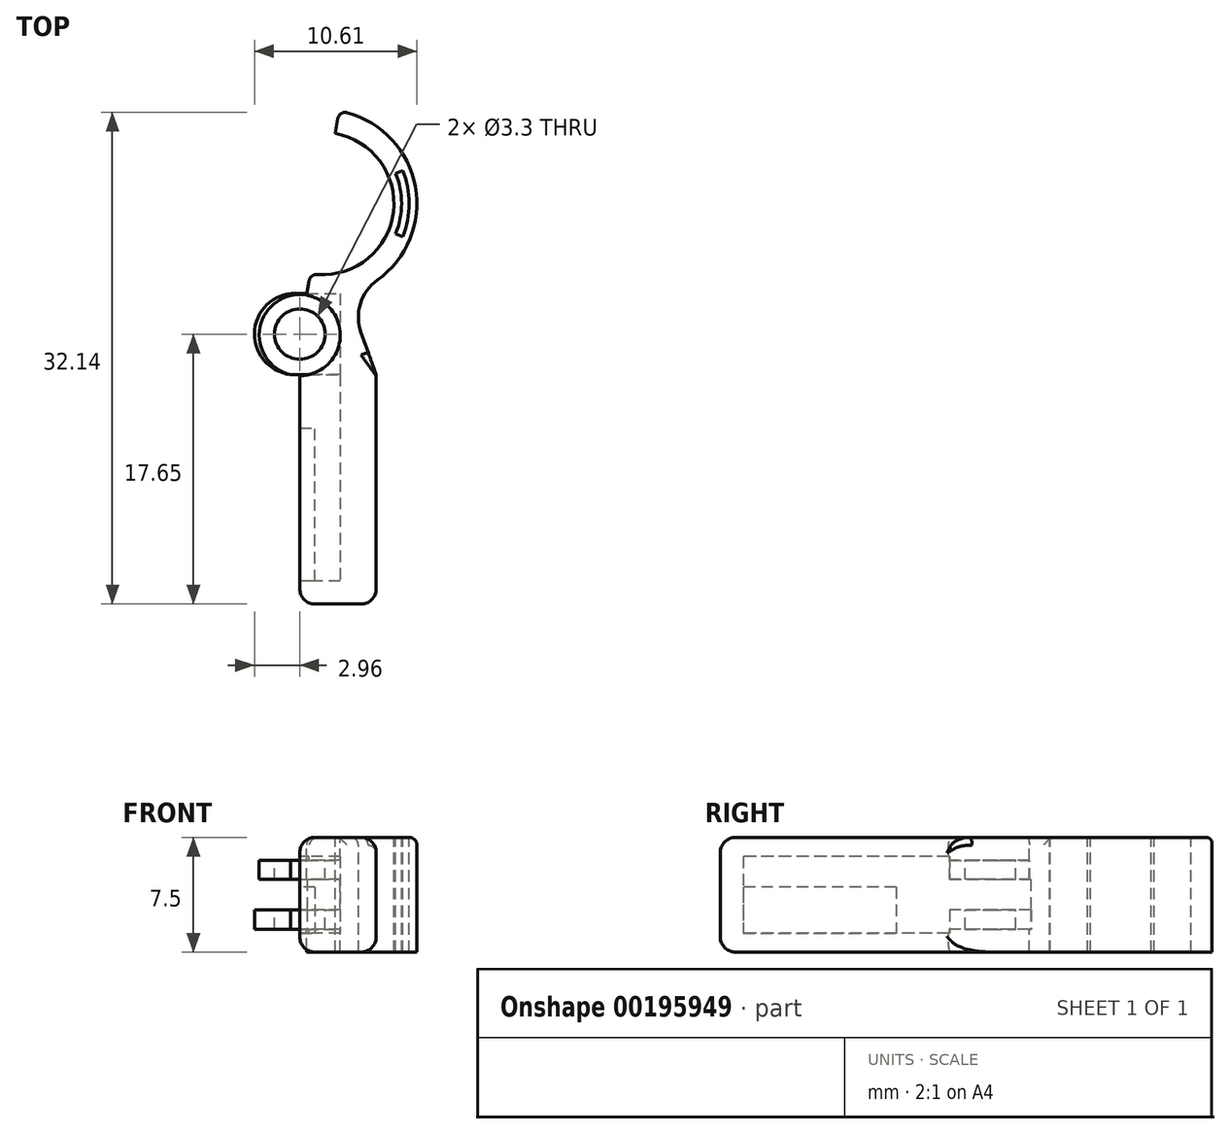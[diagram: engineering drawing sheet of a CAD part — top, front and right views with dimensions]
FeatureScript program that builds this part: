
annotation { "Feature Type Name" : "Feature", "Feature Type Description" : "" }
export const myFeature = defineFeature(function(context is Context, id is Id, definition is map)
    precondition{}
    {
        {
            var Q0;
            Q0=qCreatedBy(makeId("Front.planeOp"),FACE);
            var sketch = newSketch(context, id + "F0", { "sketchPlane" : qUnion([Q0])});
            skLineSegment(sketch, "E0.bottom", {"start": v(-2.5, 3.75) * mm, "end": v(2.5, 3.75) * mm});
            skLineSegment(sketch, "E0.top", {"start": v(-2.5, -3.75) * mm, "end": v(2.5, -3.75) * mm});
            skLineSegment(sketch, "E0.left", {"start": v(-2.5, 3.75) * mm, "end": v(-2.5, -3.75) * mm});
            skLineSegment(sketch, "E0.right", {"start": v(2.5, 3.75) * mm, "end": v(2.5, -3.75) * mm});
            skSolve(sketch);
        }
        {
            var Q0;
            Q0=makeQuery(id+"F0.imprint","IMPRINT",FACE,{"disambiguationData":[TD([[makeQuery(id+"F0.imprint","IMPRINT",EDGE,{"derivedFrom":sQuery(id+"F0.wireOp",EDGE,"E0.bottom")}),-1.0]])]});
            extrude(context, id + "F1", {"entities" : qUnion([Q0]), "oppositeDirection" : true, "depth" : 15 * mm});
        }
        {
            var Q0;
            Q0=makeQuery(id+"F1.opExtrude","SWEPT_FACE",FACE,{"disambiguationData":[OSD([sQuery(id+"F0.wireOp",EDGE,"E0.bottom")])]});
            var sketch = newSketch(context, id + "F2", { "sketchPlane" : qUnion([Q0])});
            skLineSegment(sketch, "E1", {"start": v(2.5, 15) * mm, "end": v(-2.5, 15) * mm});
            skCircle(sketch, "E2", {"center": v(-2.5, 17.58) * mm, "radius": 1.65 * mm});
            skLineSegment(sketch, "E3", {"start": v(-2.5, 32.47) * mm, "end": v(-2.5, 20.17) * mm, "construction": true});
            skLineSegment(sketch, "E4", {"start": v(2.5, 15) * mm, "end": v(0.6, 20.24) * mm});
            skArc(sketch, "E5", {"start": v(-2.5, 20.17) * mm, "mid": v(-5.08, 17.58) * mm, "end": v(-2.5, 15) * mm});
            skLineSegment(sketch, "E6.trimOffspring", {"start": v(-0.19, 30.76) * mm, "end": v(0.07, 32.24) * mm});
            skArc(sketch, "E7", {"start": v(-2.06, 20.13) * mm, "mid": v(-5.07, 17.8) * mm, "end": v(-2.5, 15) * mm});
            skLineSegment(sketch, "E8.trimOffspring", {"start": v(-2.06, 20.13) * mm, "end": v(-1.8, 21.6) * mm});
            skLineSegment(sketch, "E9", {"start": v(-0.27, 30.27) * mm, "end": v(-1.72, 22.1) * mm, "construction": true});
            skPoint(sketch, "E10", {"position": v(-1, 26.18) * mm});
            skArc(sketch, "E11", {"start": v(-2.5, 20.22) * mm, "mid": v(-2.28, 20.17) * mm, "end": v(-2.06, 20.13) * mm});
            skArc(sketch, "E12.trimOffspring", {"start": v(0.6, 20.24) * mm, "mid": v(5.15, 26.45) * mm, "end": v(0.07, 32.24) * mm});
            skArc(sketch, "E13", {"start": v(-1.8, 21.6) * mm, "mid": v(3.58, 25.38) * mm, "end": v(-0.19, 30.76) * mm});
            skSolve(sketch);
        }
        {
            var Q0;
            Q0=qSketchRegion(id+"F2",true);
            var Q1;
            Q1=makeQuery(id+"F1.opExtrude","SWEPT_FACE",FACE,{"disambiguationData":[OSD([sQuery(id+"F0.wireOp",EDGE,"E0.top")])]});
            extrude(context, id + "F3", {"entities" : qUnion([Q0]), "operationType" : NewBodyOperationType.ADD, "endBound" : BoundingType.UP_TO_SURFACE, "oppositeDirection" : true, "endBoundEntityFace" : qUnion([Q1]), "depth" : 25 * mm});
        }
        {
            var Q0;
            Q0=makeQuery(id+"F3.boolean.opBoolean","MERGE",FACE,{"derivedFrom":[makeQuery(id+"F1.opExtrude","SWEPT_FACE",FACE,{"disambiguationData":[OSD([sQuery(id+"F0.wireOp",EDGE,"E0.bottom")])]}),makeQuery(id+"F3.opExtrude","CAP_FACE",FACE,{"disambiguationData":[OSD([sQuery(id+"F2.wireOp",EDGE,"E1"),sQuery(id+"F2.wireOp",EDGE,"E2"),sQuery(id+"F2.wireOp",EDGE,"B9JCAYym-b5s2-WaWf-YfGt-LBT5zxrqjMaR"),sQuery(id+"F2.wireOp",EDGE,"Ub5ObEa3-LSRd-y38C-kyzX-ncU0hSC1jkLU"),sQuery(id+"F2.wireOp",EDGE,"msjFJeTt-mXro-ggz3-w7Y5-5ResKncMShYH"),sQuery(id+"F2.wireOp",EDGE,"pVOFhWqQ-R0tv-80Kr-So2p-xKMuH6NPngEm"),sQuery(id+"F2.wireOp",EDGE,"6c9f61bb-61ba-4d6e-9064-ecf24c568932.trimOffspring"),sQuery(id+"F2.wireOp",EDGE,"f9b7a8c3-8cce-441f-8e96-de4bfab7fc40.trimOffspring"),sQuery(id+"F2.wireOp",EDGE,"E4")])],"isStart":true})]});
            var sketch = newSketch(context, id + "F4", { "sketchPlane" : qUnion([Q0])});
            skPoint(sketch, "E14", {"position": v(-2.5, 17.65) * mm});
            skLineSegment(sketch, "E15", {"start": v(-5.15, 17.65) * mm, "end": v(-5.15, 15.22) * mm, "construction": true});
            skSolve(sketch);
        }
        {
            var Q0;
            Q0=sQuery(id+"F4.wireOp",EDGE,"E15");
            cPlane(context, id + "F5", {"entities" : qUnion([Q0]), "cplaneType" : CPlaneType.LINE_ANGLE, "offset" : 25 * mm, "angle" : 90 * degree, "width" : 150 * mm, "height" : 150 * mm});
        }
        {
            var Q0;
            Q0=qCreatedBy(id+"F5.planeOp",FACE);
            var sketch = newSketch(context, id + "F6", { "sketchPlane" : qUnion([Q0])});
            skLineSegment(sketch, "E16.left", {"start": v(20.3, -2.25) * mm, "end": v(20.3, 2.25) * mm});
            skLineSegment(sketch, "E17", {"start": v(20.3, 2.25) * mm, "end": v(15, 2.25) * mm});
            skLineSegment(sketch, "E18", {"start": v(20.3, -2.25) * mm, "end": v(15, -2.25) * mm});
            skLineSegment(sketch, "E19.bottom", {"start": v(15, 2.5) * mm, "end": v(1.5, 2.5) * mm});
            skLineSegment(sketch, "E19.top", {"start": v(15, -2.5) * mm, "end": v(1.5, -2.5) * mm});
            skLineSegment(sketch, "E19.left", {"start": v(15, 2.5) * mm, "end": v(15, 2.25) * mm});
            skLineSegment(sketch, "E19.right", {"start": v(1.5, 2.5) * mm, "end": v(1.5, -2.5) * mm});
            skLineSegment(sketch, "E20.trimOffspring", {"start": v(15, -2.25) * mm, "end": v(15, -2.5) * mm});
            skSolve(sketch);
        }
        {
            var Q0;
            Q0=qSketchRegion(id+"F6",true);
            extrude(context, id + "F7", {"entities" : qUnion([Q0]), "operationType" : NewBodyOperationType.REMOVE, "depth" : 5.3 * mm});
        }
        {
            var Q0;
            {var subQ0=sQuery(id+"F0.wireOp",EDGE,"E0.bottom");Q0=makeQuery(id+"F4.imprint","IMPRINT",FACE,{"disambiguationData":[TD([[makeQuery(id+"F4.imprint","IMPRINT",EDGE,{"derivedFrom":makeQuery(id+"F1.opExtrude","CAP_EDGE",EDGE,{"disambiguationData":[OSD([subQ0])],"isStart":true})}),1.0]])]});}
            var sketch = newSketch(context, id + "F8", { "sketchPlane" : qUnion([Q0])});
            skPoint(sketch, "E21.orphan", {"position": v(-1.9, 31.06) * mm});
            skPoint(sketch, "E22.orphan", {"position": v(-1.7, 32.55) * mm});
            skPoint(sketch, "E23.orphan", {"position": v(-3.1, 21.84) * mm});
            skPoint(sketch, "E24.orphan", {"position": v(0.32, 20.99) * mm});
            skPoint(sketch, "E25.orphan", {"position": v(0.07, 32.24) * mm});
            skPoint(sketch, "E26.0.start.orphan", {"position": v(0.6, 20.24) * mm});
            skArc(sketch, "E27.0", {"start": v(4.22, 24.02) * mm, "mid": v(4.65, 26.18) * mm, "end": v(4.22, 28.35) * mm});
            skArc(sketch, "E28.0", {"start": v(3.76, 24.21) * mm, "mid": v(4.15, 26.18) * mm, "end": v(3.76, 28.16) * mm});
            skLineSegment(sketch, "E29", {"start": v(3.76, 28.16) * mm, "end": v(4.22, 28.35) * mm});
            skLineSegment(sketch, "E30", {"start": v(3.76, 24.21) * mm, "end": v(4.22, 24.02) * mm});
            skLineSegment(sketch, "E31", {"start": v(-1, 26.18) * mm, "end": v(7.11, 26.18) * mm, "construction": true});
            skSolve(sketch);
        }
        {
            var Q0;
            Q0=qSketchRegion(id+"F8",true);
            extrude(context, id + "F9", {"entities" : qUnion([Q0]), "operationType" : NewBodyOperationType.REMOVE, "endBound" : BoundingType.THROUGH_ALL, "oppositeDirection" : true, "depth" : 25 * mm});
        }
        {
            var Q0;
            {var subQ0=sQuery(id+"F0.wireOp",EDGE,"E0.bottom");Q0=makeQuery(id+"F4.imprint","IMPRINT",FACE,{"disambiguationData":[TD([[makeQuery(id+"F4.imprint","IMPRINT",EDGE,{"derivedFrom":makeQuery(id+"F1.opExtrude","CAP_EDGE",EDGE,{"disambiguationData":[OSD([subQ0])],"isStart":true})}),1.0]])]});}
            var sketch = newSketch(context, id + "F10", { "sketchPlane" : qUnion([Q0])});
            skCircle(sketch, "E32", {"center": v(-2.5, 17.58) * mm, "radius": 2.65 * mm});
            skSolve(sketch);
        }
        {
            var Q0;
            Q0 = qSketchRegion(id + "F10", true);
            var Q1;
            {var subQ0=sQuery(id+"F0.wireOp",EDGE,"E0.top");Q1=makeQuery(id+"F3.boolean.opBoolean","MERGE",FACE,{"derivedFrom":[makeQuery(id+"F1.opExtrude","SWEPT_FACE",FACE,{"disambiguationData":[OSD([subQ0])]}),makeQuery(id+"F3.opExtrude","CAP_FACE",FACE,{"disambiguationData":[OSD([subQ0])],"isStart":false})]});}
            extrude(context, id + "F11", {"entities" : qUnion([Q0]), "operationType" : NewBodyOperationType.REMOVE, "endBound" : BoundingType.UP_TO_SURFACE, "oppositeDirection" : true, "endBoundEntityFace" : qUnion([Q1]), "depth" : 1.5 * mm});
        }
        {
            var Q0;
            {var subQ0=sQuery(id+"F6.wireOp",EDGE,"E19.left");var subQ1=sQuery(id+"F6.wireOp",EDGE,"E17");var subQ2=makeQuery(id+"F7.boolean.opBoolean","COPY",FACE,{"derivedFrom":makeQuery(id+"F7.opExtrude","SWEPT_FACE",FACE,{"disambiguationData":[OSD([subQ1])]})});Q0=makeQuery(id+"F11.boolean.opBoolean","SPLIT",FACE,{"disambiguationData":[TD([makeQuery(id+"F7.boolean.opBoolean","COPY",FACE,{"derivedFrom":makeQuery(id+"F7.opExtrude","SWEPT_FACE",FACE,{"disambiguationData":[OSD([subQ0])]})})])],"derivedFrom":subQ2});}
            var sketch = newSketch(context, id + "F12", { "sketchPlane" : qUnion([Q0])});
            skLineSegment(sketch, "E33", {"start": v(-3.1, -15) * mm, "end": v(0.15, -15) * mm});
            skPoint(sketch, "E34.2.end.orphan", {"position": v(2.5, 0) * mm});
            skPoint(sketch, "E34.1.end.orphan", {"position": v(-2.5, 0) * mm});
            skLineSegment(sketch, "E35.0", {"start": v(0.15, -17.58) * mm, "end": v(0.15, -15) * mm});
            skLineSegment(sketch, "E35.1", {"start": v(0.15, -20.3) * mm, "end": v(0.15, -17.58) * mm});
            skLineSegment(sketch, "E35.2", {"start": v(0.15, -20.3) * mm, "end": v(-2.03, -20.3) * mm});
            skPoint(sketch, "E34.0.start.orphan", {"position": v(2.5, -15) * mm});
            skPoint(sketch, "E36.start.orphan", {"position": v(0.6, -20.24) * mm});
            skPoint(sketch, "E37.orphan", {"position": v(-2.5, -20.3) * mm});
            skArc(sketch, "E38", {"start": v(-3.1, -15) * mm, "mid": v(-5.1, -18.1) * mm, "end": v(-2.05, -20.2) * mm});
            skLineSegment(sketch, "E39.0", {"start": v(-2.05, -20.2) * mm, "end": v(-2.03, -20.3) * mm});
            skSolve(sketch);
        }
        {
            var Q0;
            Q0 = qSketchRegion(id + "F12", true);
            extrude(context, id + "F13", {"entities" : qUnion([Q0]), "operationType" : NewBodyOperationType.ADD, "depth" : 1.25 * mm});
        }
        {
            var Q0;
            {var subQ0=sQuery(id+"F6.wireOp",EDGE,"E20.trimOffspring");var subQ1=sQuery(id+"F6.wireOp",EDGE,"E18");var subQ2=makeQuery(id+"F7.boolean.opBoolean","COPY",FACE,{"derivedFrom":makeQuery(id+"F7.opExtrude","SWEPT_FACE",FACE,{"disambiguationData":[OSD([subQ1])]})});Q0=makeQuery(id+"F11.boolean.opBoolean","SPLIT",FACE,{"disambiguationData":[TD([makeQuery(id+"F7.boolean.opBoolean","COPY",FACE,{"derivedFrom":makeQuery(id+"F7.opExtrude","SWEPT_FACE",FACE,{"disambiguationData":[OSD([subQ0])]})})])],"derivedFrom":subQ2});}
            var sketch = newSketch(context, id + "F14", { "sketchPlane" : qUnion([Q0])});
            skLineSegment(sketch, "E40.0.0", {"start": v(0.15, 15) * mm, "end": v(-3.1, 15) * mm});
            skArc(sketch, "E40.0.1", {"start": v(-3.1, 15) * mm, "mid": v(-5.45, 17.95) * mm, "end": v(-2.5, 20.3) * mm});
            skLineSegment(sketch, "E40.0.2", {"start": v(-2.5, 20.3) * mm, "end": v(0.15, 20.3) * mm});
            skLineSegment(sketch, "E40.0.3", {"start": v(0.15, 20.3) * mm, "end": v(0.15, 15) * mm});
            skSolve(sketch);
        }
        {
            var Q0;
            Q0 = qSketchRegion(id + "F14", true);
            extrude(context, id + "F15", {"entities" : qUnion([Q0]), "operationType" : NewBodyOperationType.ADD, "depth" : 1.25 * mm});
        }
        {
            var Q0;
            Q0=makeQuery(id+"F13.opExtrude","CAP_FACE",FACE,{"disambiguationData":[OSD([sQuery(id+"F12.wireOp",EDGE,"E33"),sQuery(id+"F12.wireOp",EDGE,"E35.0"),sQuery(id+"F12.wireOp",EDGE,"E35.1"),sQuery(id+"F12.wireOp",EDGE,"E35.2"),sQuery(id+"F12.wireOp",EDGE,"EVlaqA6L-qsqQ-DwHj-K3Q7-744cLPcn2Ljy")])],"isStart":true});
            var sketch = newSketch(context, id + "F16", { "sketchPlane" : qUnion([Q0])});
            skCircle(sketch, "E41", {"center": v(-2.5, 17.65) * mm, "radius": 1.65 * mm});
            skSolve(sketch);
        }
        {
            var Q0;
            Q0=makeQuery(id+"F16.imprint","IMPRINT",FACE,{"disambiguationData":[TD([[makeQuery(id+"F16.imprint","IMPRINT",EDGE,{"derivedFrom":sQuery(id+"F16.wireOp",EDGE,"E41")}),1.0]])]});
            extrude(context, id + "F17", {"entities" : qUnion([Q0]), "operationType" : NewBodyOperationType.REMOVE, "endBound" : BoundingType.THROUGH_ALL, "oppositeDirection" : true, "depth" : 25 * mm});
        }
        {
            var Q0;
            Q0=makeQuery(id+"F3.opExtrude","SWEPT_EDGE",EDGE,{"disambiguationData":[OSD([sQuery(id+"F2.wireOp",EDGE,"E4"),sQuery(id+"F2.wireOp",EDGE,"K92U0NBN-zdy9-IzVP-x1tL-mb1lYgoXCjgz")])]});
            fillet(context, id + "F18", {"entities" : qUnion([Q0]), "radius" : 3 * mm, "tangentPropagation" : true, "allowEdgeOverflow" : false});
        }
        {
            var Q0;
            Q0=makeQuery(id+"F7.boolean.opBoolean","COPY",FACE,{"derivedFrom":makeQuery(id+"F7.opExtrude","SWEPT_FACE",FACE,{"disambiguationData":[OSD([sQuery(id+"F6.wireOp",EDGE,"E19.top")])]})});
            var sketch = newSketch(context, id + "F19", { "sketchPlane" : qUnion([Q0])});
            skPoint(sketch, "E42.oppositeSnap0", {"position": v(-1.5, 1.5) * mm});
            skLineSegment(sketch, "E42.bottom", {"start": v(-2.5, 1.5) * mm, "end": v(-1.5, 1.5) * mm});
            skLineSegment(sketch, "E42.top", {"start": v(-2.5, 11.5) * mm, "end": v(-1.5, 11.5) * mm});
            skLineSegment(sketch, "E42.left", {"start": v(-2.5, 1.5) * mm, "end": v(-2.5, 11.5) * mm});
            skLineSegment(sketch, "E42.right", {"start": v(-1.5, 1.5) * mm, "end": v(-1.5, 11.5) * mm});
            skSolve(sketch);
        }
        {
            var Q0;
            Q0 = qSketchRegion(id + "F19", true);
            extrude(context, id + "F20", {"entities" : qUnion([Q0]), "operationType" : NewBodyOperationType.ADD, "depth" : 3 * mm});
        }
        {
            var Q0;
            Q0=makeQuery(id+"F1.opExtrude","SWEPT_EDGE",EDGE,{"disambiguationData":[OSD([sQuery(id+"F0.wireOp",EDGE,"E0.bottom"),sQuery(id+"F0.wireOp",EDGE,"E0.right")])]});
            var Q1;
            Q1=makeQuery(id+"F1.opExtrude","CAP_FACE",FACE,{"disambiguationData":[OSD([sQuery(id+"F0.wireOp",EDGE,"E0.bottom"),sQuery(id+"F0.wireOp",EDGE,"E0.top"),sQuery(id+"F0.wireOp",EDGE,"E0.left"),sQuery(id+"F0.wireOp",EDGE,"E0.right")])],"isStart":true});
            var Q2;
            Q2=makeQuery(id+"F1.opExtrude","SWEPT_FACE",FACE,{"disambiguationData":[OSD([sQuery(id+"F0.wireOp",EDGE,"E0.right")])]});
            var Q3;
            Q3=makeQuery(id+"F1.opExtrude","SWEPT_EDGE",EDGE,{"disambiguationData":[OSD([sQuery(id+"F0.wireOp",EDGE,"E0.top"),sQuery(id+"F0.wireOp",EDGE,"E0.left")])]});
            var Q4;
            Q4=makeQuery(id+"F1.opExtrude","SWEPT_EDGE",EDGE,{"disambiguationData":[OSD([sQuery(id+"F0.wireOp",EDGE,"E0.bottom"),sQuery(id+"F0.wireOp",EDGE,"E0.left")])]});
            fillet(context, id + "F21", {"entities" : qUnion([Q0, Q1, Q2, Q3, Q4]), "radius" : 1 * mm, "tangentPropagation" : true, "allowEdgeOverflow" : false});
        }
        {
            var Q0;
            Q0=makeQuery(id+"F3.opExtrude","SWEPT_EDGE",EDGE,{"disambiguationData":[OSD([sQuery(id+"F2.wireOp",EDGE,"E6.trimOffspring"),sQuery(id+"F2.wireOp",EDGE,"E12.trimOffspring")])]});
            var Q1;
            Q1=makeQuery(id+"F3.opExtrude","CAP_EDGE",EDGE,{"disambiguationData":[OSD([sQuery(id+"F2.wireOp",EDGE,"E12.trimOffspring")])],"isStart":true});
            var Q2;
            Q2=makeQuery(id+"F3.opExtrude","TWEAK_EDGE",EDGE,{"derivedFrom":[makeQuery(id+"F1.opExtrude","SWEPT_FACE",FACE,{"disambiguationData":[OSD([sQuery(id+"F0.wireOp",EDGE,"E0.top")])]}),makeQuery(id+"F2.imprint","IMPRINT",EDGE,{"derivedFrom":sQuery(id+"F2.wireOp",EDGE,"E12.trimOffspring")})]});
            var Q3;
            Q3=makeQuery(id+"F3.opExtrude","SWEPT_EDGE",EDGE,{"disambiguationData":[OSD([sQuery(id+"F2.wireOp",EDGE,"E8.trimOffspring"),sQuery(id+"F2.wireOp",EDGE,"E13")])]});
            var Q4;
            Q4=makeQuery(id+"F3.opExtrude","CAP_EDGE",EDGE,{"disambiguationData":[OSD([sQuery(id+"F2.wireOp",EDGE,"E8.trimOffspring")])],"isStart":true});
            var Q5;
            Q5=makeQuery(id+"F3.opExtrude","TWEAK_EDGE",EDGE,{"derivedFrom":[makeQuery(id+"F1.opExtrude","SWEPT_FACE",FACE,{"disambiguationData":[OSD([sQuery(id+"F0.wireOp",EDGE,"E0.top")])]}),makeQuery(id+"F2.imprint","IMPRINT",EDGE,{"derivedFrom":sQuery(id+"F2.wireOp",EDGE,"E8.trimOffspring")})]});
            fillet(context, id + "F22", {"entities" : qUnion([Q0, Q1, Q2, Q3, Q4, Q5]), "radius" : .5 * mm, "tangentPropagation" : true, "allowEdgeOverflow" : false});
        }
    });
